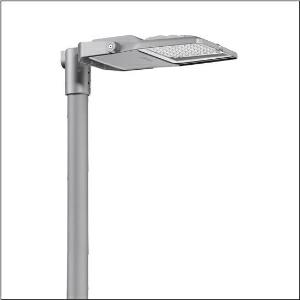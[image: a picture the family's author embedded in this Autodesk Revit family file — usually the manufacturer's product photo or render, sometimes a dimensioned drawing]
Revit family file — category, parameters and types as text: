
# Revit family: floodlight_fl_21_iq_mini___pl52_5xa7772b2d3a_55c6
name_source: partatom
category: Lighting Fixtures
units: mm (PartAtom-declared; Revit-internal decimal feet)

## family parameters
Cut with Voids When Loaded = No
Host = Face
Light Source = No
Part Type = Normal
Room Calculation Point = No
Round Connector Dimension = Use Diameter
Shared = No

## types (1)
- --- (1 x LED, 6240 lm, 45.5 W, 3000K)
    Apparent Load = 46 VA
    CIE Flux Codes = 26 60 98 100 100
    Color Rendering = 70
    Color Temperature = 3000K
    Default Elevation = 1800 mm
    Description = Floodlight FL 21 iQ mini, floodlight, primary light control with lens, of PMMA, primary optical cover: protective disc, of toughened safety glass, transparent, light distribution: PL52, light emission: direct distribution, installation type: surface-mounted, LED, High Power LED, rated luminous flux: 6.240lm, luminous efficacy: 137lm/W, light colour: 730, colour temperature: 3000K, control: Auto-Match, Temp-Guard, Night-Set, Smart-Wire, Desk-Remote (wireless, voltage-free reading and setting of iQ features in the workshop via application-optimized NFC function/RFID function), optimised constant luminous flux control (CLO 2.0), Light-Fading, Lumen-Switch, with terminal, 6-pole, mains connection: 220..240V, AC, 50/60Hz, start of lifetime: 46W, end of service life: 48W, reduction: 22W, luminaire housing, of diecast aluminium, powder-coated, Siteco® metallic grey (DB 702S), corrosivity category C5 mid according to DIN EN ISO 12944, sealing non-destructively replaceable, please order mast flange separately, mast bracket, of steel, galvanised, powder-coated, protection rating (complete): IP66, insulation class (complete): insulation class II (safety insulation), certification: CE, ENEC, VDE, protection symbol: D, impact resistance: IK08, permissible operating ambient temperature: -40..+40°C, permissible operating ambient temperature for outdoor applications: -40..+50°C, standard: DIN EN 12944, LABS conformity tested according to VDMA 24364:2018-05, packaging unit: 1 piece

Light Distribution: PL52
    Height = 70 mm
    Lamp = 1 x LED
    Lamp Light Flux = 6240 lm
    Lamp Power = 45.5 W
    Lamp count = 1
    Length = 485 mm
    Luminous efficacy = 137 lm/W
    Manufacturer = Siteco
    ModVariant = No
    Model = 5XA7772B2D3A
    Number of Poles = 1
    OnlyDefault = Yes
    Power Factor = 1
    Product Name = Floodlight FL 21 iQ mini | PL52
    Product group = floodlight | pylon annexe
    ProductGroupID = 6200
    Protection Class = Protection class II
    Protection Degree = IP 66
    RLX_Detail_Level = 1
    RLX_Emergency_Light_Flux = 0 lm
    RLX_Emergency_Type = 0
    RLX_Emergency_Type_DB = No
    RlxData = <blob elided: 101401 chars, md5=1d69f57e>
    Socket = socket
    Standby Power = 0 W
    System Light Flux = 6240 lm
    System Power = 46 W
    Type Comments = factory setting: luminous flux: 100 % | dim-lin: 254 | 463 mA
    Type Image = l_1007125.jpg
    URL = http://relux.com
    VarID = @adj_097143
    Voltage = 0 V
    Weight = 0.00 kg
    Width = 337 mm

## geometry (parser evidence)
native form markers: Blend x4, Sweep x13
no freeform markers — native parametric forms only
